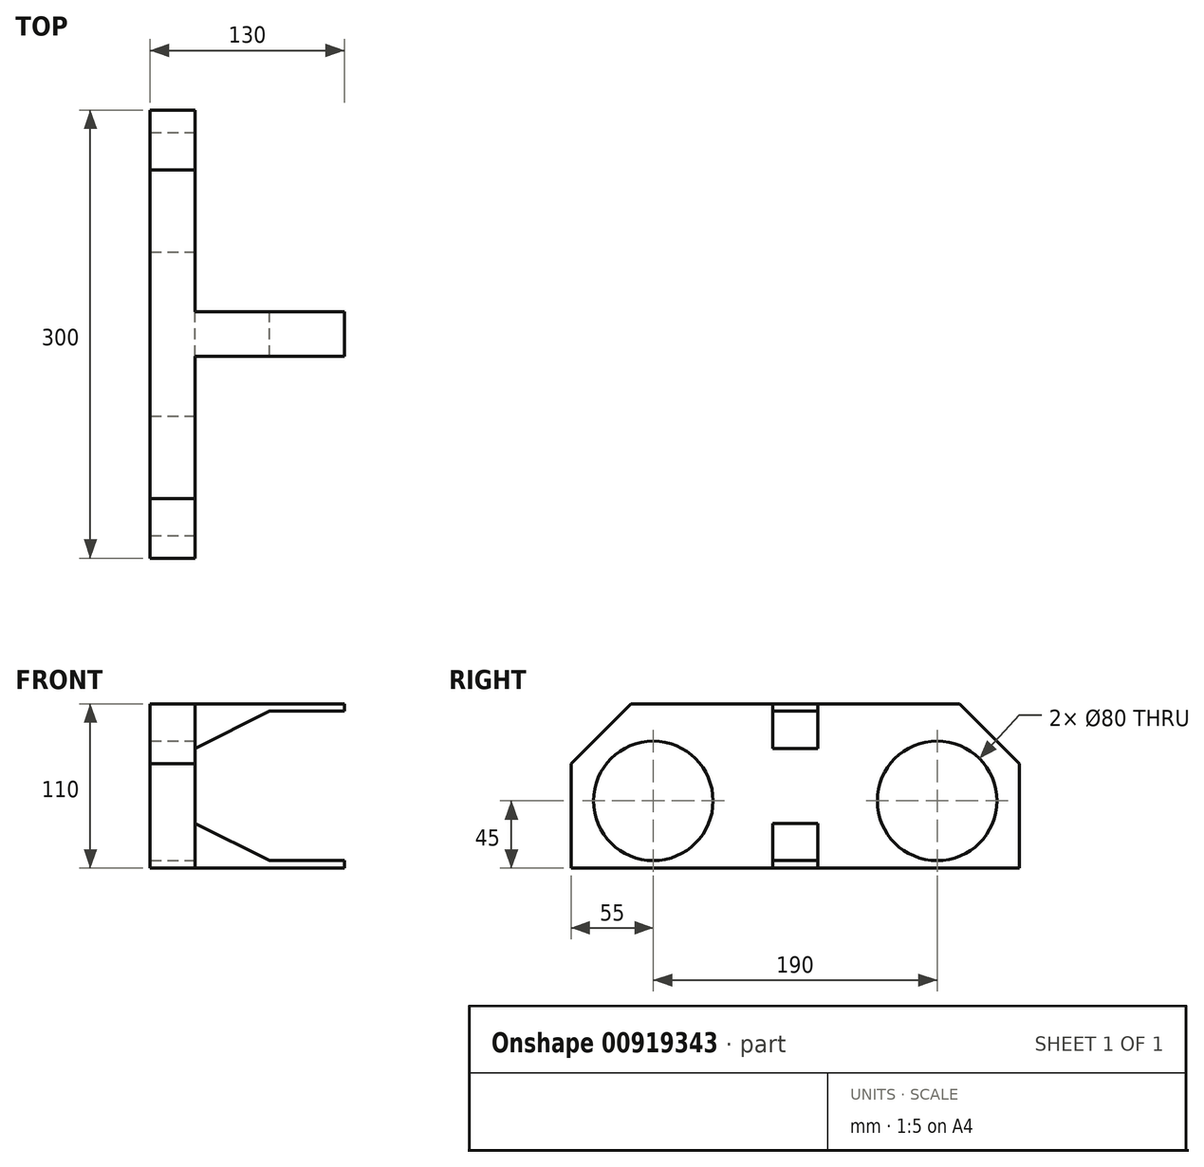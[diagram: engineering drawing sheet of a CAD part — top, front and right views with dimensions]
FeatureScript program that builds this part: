
annotation { "Feature Type Name" : "Feature", "Feature Type Description" : "" }
export const myFeature = defineFeature(function(context is Context, id is Id, definition is map)
    precondition{}
    {
        {
            var Q0;
            Q0=qCreatedBy(makeId("Right.planeOp"),FACE);
            var sketch = newSketch(context, id + "F0", { "sketchPlane" : qUnion([Q0])});
            skLineSegment(sketch, "E0.bottom", {"start": v(0, 0) * mm, "end": v(300, 0) * mm});
            skLineSegment(sketch, "E0.top", {"start": v(0, 110) * mm, "end": v(300, 110) * mm});
            skLineSegment(sketch, "E0.left", {"start": v(0, 0) * mm, "end": v(0, 110) * mm});
            skLineSegment(sketch, "E0.right", {"start": v(300, 0) * mm, "end": v(300, 110) * mm});
            skSolve(sketch);
        }
        {
            var Q0;
            Q0=makeQuery(id+"F0.imprint","IMPRINT",FACE,{"disambiguationData":[TD([[makeQuery(id+"F0.imprint","IMPRINT",EDGE,{"derivedFrom":sQuery(id+"F0.wireOp",EDGE,"E0.bottom")}),1.0]])]});
            extrude(context, id + "F1", {"entities" : qUnion([Q0]), "depth" : 30 * mm, "offsetDistance" : 25 * mm});
        }
        {
            var Q0;
            Q0=makeQuery(id+"F1.opExtrude","CAP_FACE",FACE,{"disambiguationData":[OSD([sQuery(id+"F0.wireOp",EDGE,"E0.bottom"),sQuery(id+"F0.wireOp",EDGE,"E0.top"),sQuery(id+"F0.wireOp",EDGE,"E0.left"),sQuery(id+"F0.wireOp",EDGE,"E0.right")])],"isStart":false});
            var sketch = newSketch(context, id + "F2", { "sketchPlane" : qUnion([Q0])});
            skCircle(sketch, "E1", {"center": v(55, 45) * mm, "radius": 40 * mm});
            skCircle(sketch, "E2", {"center": v(245, 45) * mm, "radius": 40 * mm});
            skSolve(sketch);
        }
        {
            var Q0;
            Q0 = qSketchRegion(id + "F2", true);
            extrude(context, id + "F3", {"entities" : qUnion([Q0]), "operationType" : NewBodyOperationType.REMOVE, "endBound" : BoundingType.UP_TO_NEXT, "oppositeDirection" : true, "depth" : 25 * mm, "offsetDistance" : 25 * mm});
        }
        {
            var Q0;
            Q0=makeQuery(id+"F1.opExtrude","CAP_FACE",FACE,{"disambiguationData":[OSD([sQuery(id+"F0.wireOp",EDGE,"E0.bottom"),sQuery(id+"F0.wireOp",EDGE,"E0.top"),sQuery(id+"F0.wireOp",EDGE,"E0.left"),sQuery(id+"F0.wireOp",EDGE,"E0.right")])],"isStart":false});
            var sketch = newSketch(context, id + "F4", { "sketchPlane" : qUnion([Q0])});
            skLineSegment(sketch, "E3.bottom", {"start": v(135, 110) * mm, "end": v(165, 110) * mm});
            skLineSegment(sketch, "E3.top", {"start": v(135, 80) * mm, "end": v(165, 80) * mm});
            skLineSegment(sketch, "E3.left", {"start": v(135, 110) * mm, "end": v(135, 80) * mm});
            skLineSegment(sketch, "E3.right", {"start": v(165, 110) * mm, "end": v(165, 80) * mm});
            skLineSegment(sketch, "E4.bottom", {"start": v(135, 0) * mm, "end": v(165, 0) * mm});
            skLineSegment(sketch, "E4.top", {"start": v(135, 30) * mm, "end": v(165, 30) * mm});
            skLineSegment(sketch, "E4.left", {"start": v(135, 0) * mm, "end": v(135, 30) * mm});
            skLineSegment(sketch, "E4.right", {"start": v(165, 0) * mm, "end": v(165, 30) * mm});
            skSolve(sketch);
        }
        {
            var Q0;
            Q0 = qSketchRegion(id + "F4", true);
            extrude(context, id + "F5", {"entities" : qUnion([Q0]), "operationType" : NewBodyOperationType.ADD, "depth" : 100 * mm, "offsetDistance" : 25 * mm});
        }
        {
            var Q0;
            Q0=makeQuery(id+"F5.opExtrude","SWEPT_FACE",FACE,{"disambiguationData":[OSD([sQuery(id+"F4.wireOp",EDGE,"E3.right")])]});
            var sketch = newSketch(context, id + "F6", { "sketchPlane" : qUnion([Q0])});
            skLineSegment(sketch, "E5", {"start": v(-130, 30) * mm, "end": v(-30, 30) * mm});
            skLineSegment(sketch, "E6", {"start": v(-130, 105) * mm, "end": v(-130, 110) * mm});
            skLineSegment(sketch, "E7", {"start": v(-130, 105) * mm, "end": v(-80, 105) * mm});
            skLineSegment(sketch, "E8", {"start": v(-80, 105) * mm, "end": v(-30, 80) * mm});
            skLineSegment(sketch, "E9", {"start": v(-130, 5) * mm, "end": v(-130, 0) * mm});
            skLineSegment(sketch, "E10", {"start": v(-130, 0) * mm, "end": v(-30, 0) * mm});
            skLineSegment(sketch, "E11", {"start": v(-130, 5) * mm, "end": v(-80, 5) * mm});
            skLineSegment(sketch, "E12", {"start": v(-80, 5) * mm, "end": v(-30, 30) * mm});
            skLineSegment(sketch, "E13", {"start": v(-130, 5) * mm, "end": v(-130, 30) * mm});
            skSolve(sketch);
        }
        {
            var Q0;
            {var subQ0=sQuery(id+"F6.wireOp",EDGE,"E7");Q0=makeQuery(id+"F6.imprint","IMPRINT",FACE,{"disambiguationData":[TD([[makeQuery(id+"F6.imprint","IMPRINT",EDGE,{"derivedFrom":subQ0}),-1.0]])]});}
            var Q1;
            Q1=makeQuery(id+"F6.imprint","IMPRINT",FACE,{"disambiguationData":[TD([[makeQuery(id+"F6.imprint","IMPRINT",EDGE,{"derivedFrom":sQuery(id+"F6.wireOp",EDGE,"E5")}),-1.0]])]});
            extrude(context, id + "F7", {"entities" : qUnion([Q0, Q1]), "operationType" : NewBodyOperationType.REMOVE, "endBound" : BoundingType.UP_TO_NEXT, "oppositeDirection" : true, "depth" : 25 * mm, "offsetDistance" : 25 * mm});
        }
        {
            var Q0;
            Q0=makeQuery(id+"F1.opExtrude","SWEPT_EDGE",EDGE,{"disambiguationData":[OSD([sQuery(id+"F0.wireOp",EDGE,"E0.top"),sQuery(id+"F0.wireOp",EDGE,"E0.left")])]});
            var Q1;
            Q1=makeQuery(id+"F1.opExtrude","SWEPT_EDGE",EDGE,{"disambiguationData":[OSD([sQuery(id+"F0.wireOp",EDGE,"E0.top"),sQuery(id+"F0.wireOp",EDGE,"E0.right")])]});
            chamfer(context, id + "F8", {"entities" : qUnion([Q0, Q1]), "width" : 40 * mm, "tangentPropagation" : true});
        }
    });
